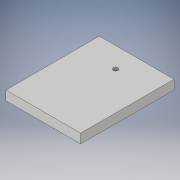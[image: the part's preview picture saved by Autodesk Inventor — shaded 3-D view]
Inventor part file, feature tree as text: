
AUTODESK INVENTOR PART (.ipt)
format: ipt  version: 2019.4 (Build 234330000, 330)  size: 95,744 bytes
history: native  units: mm
features: sketch x2, extrude x1, hole x1
ambient origin geometry x8: Origin, YZ Plane, XZ Plane, XY Plane, X Axis, Y Axis, Z Axis, Center Point
bodies: Solid1 (feature_tree)
feature tree (4):
  extrude  "Extrusion1"  Depth=100.0mm
  hole  "Hole1"  [1 undecoded]
  sketch  "Sketch1"  dims[d0=80.0mm d1=100.0mm]
  sketch  "Sketch2"  dims[d2=10.0mm d3=0.0mm d4=5.0mm d5=6.0mm d6=4.0mm d7=2.0mm d8=90.0deg d9=8.0mm d10=20.594885mm d11=0.75mm d12=20.594885mm d13=0.0625mm d14=0.75mm d15=0.375mm]
note: 1 required parameter value undecoded (feature->parameter linkage not recoverable at this tier; creation-order binding heuristic only, values carry confidence <= 0.55)
